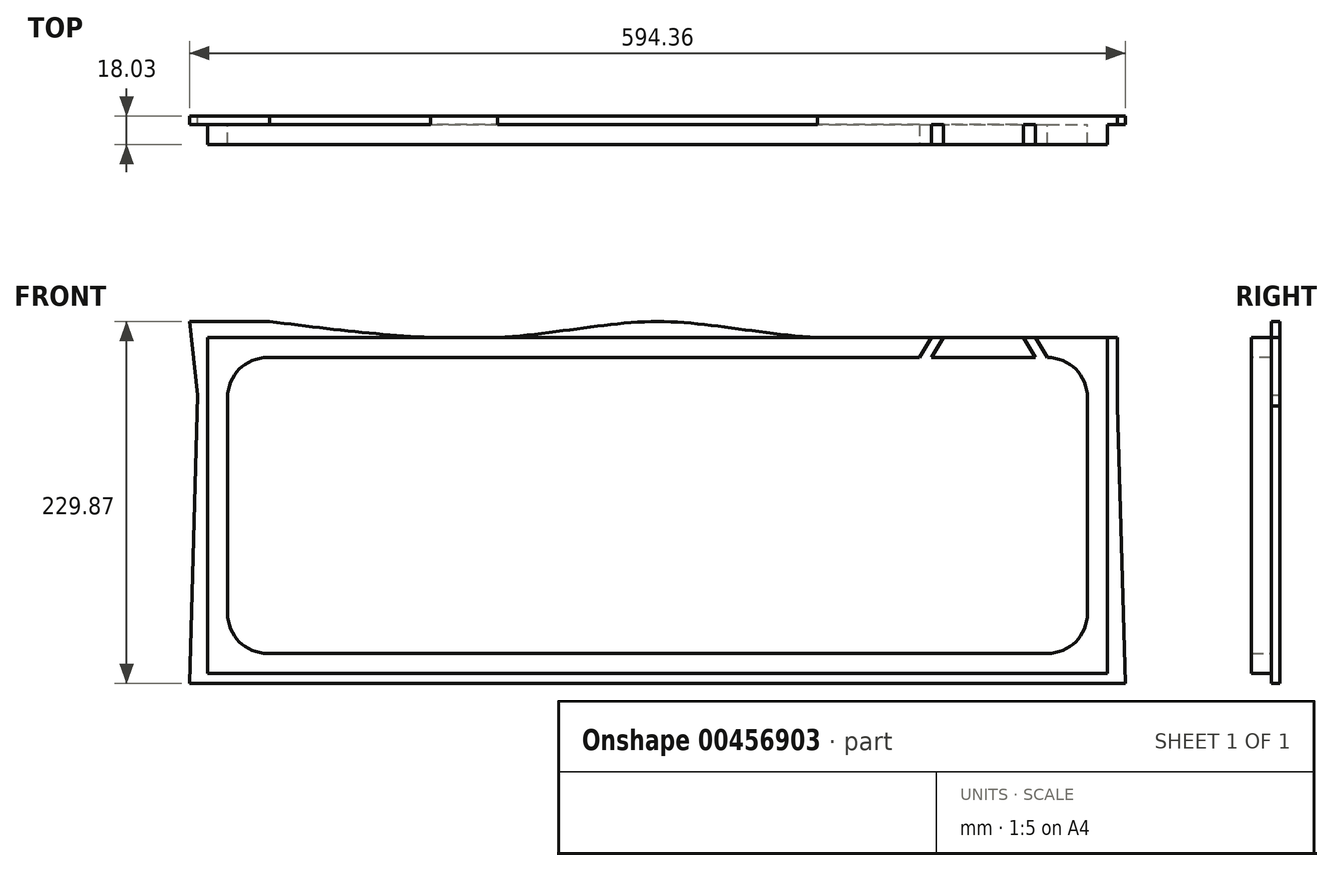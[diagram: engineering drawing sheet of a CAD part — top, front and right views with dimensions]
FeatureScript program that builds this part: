
annotation { "Feature Type Name" : "Feature", "Feature Type Description" : "" }
export const myFeature = defineFeature(function(context is Context, id is Id, definition is map)
    precondition{}
    {
        {
            var Q0;
            Q0=qCreatedBy(makeId("Front.planeOp"),FACE);
            var sketch = newSketch(context, id + "F0", { "sketchPlane" : qUnion([Q0])});
            skLineSegment(sketch, "E0.bottom", {"start": v(0, 0) * mm, "end": v(-584.2, 0) * mm});
            skLineSegment(sketch, "E0.top", {"start": v(0, 219.7) * mm, "end": v(-584.2, 219.7) * mm});
            skLineSegment(sketch, "E0.left", {"start": v(0, 0) * mm, "end": v(0, 219.7) * mm});
            skLineSegment(sketch, "E0.right", {"start": v(-584.2, 0) * mm, "end": v(-584.2, 219.7) * mm});
            skPoint(sketch, "E1", {"position": v(-292.1, 219.7) * mm});
            skSolve(sketch);
        }
        {
            var Q0;
            Q0=makeQuery(id+"F0.imprint","IMPRINT",FACE,{"disambiguationData":[TD([[makeQuery(id+"F0.imprint","IMPRINT",EDGE,{"derivedFrom":sQuery(id+"F0.wireOp",EDGE,"E0.bottom")}),-1.0]])]});
            extrude(context, id + "F1", {"entities" : qUnion([Q0]), "depth" : 5.33 * mm});
        }
        {
            var Q0;
            Q0=makeQuery(id+"F1.opExtrude","CAP_FACE",FACE,{"disambiguationData":[OSD([sQuery(id+"F0.wireOp",EDGE,"E0.bottom"),sQuery(id+"F0.wireOp",EDGE,"E0.top"),sQuery(id+"F0.wireOp",EDGE,"E0.left"),sQuery(id+"F0.wireOp",EDGE,"E0.right")])],"isStart":false});
            var sketch = newSketch(context, id + "F2", { "sketchPlane" : qUnion([Q0])});
            skLineSegment(sketch, "E2", {"start": v(-577.85, 219.7) * mm, "end": v(-577.85, 6.35) * mm});
            skLineSegment(sketch, "E3", {"start": v(-577.85, 6.35) * mm, "end": v(-6.35, 6.35) * mm});
            skLineSegment(sketch, "E4", {"start": v(-6.35, 6.35) * mm, "end": v(-6.35, 219.71) * mm});
            skLineSegment(sketch, "E5", {"start": v(-6.35, 219.71) * mm, "end": v(-577.85, 219.7) * mm});
            skLineSegment(sketch, "E6", {"start": v(-565.15, 207) * mm, "end": v(-565.15, 19.05) * mm});
            skLineSegment(sketch, "E7", {"start": v(-565.15, 19.05) * mm, "end": v(-19.05, 19.05) * mm});
            skLineSegment(sketch, "E8", {"start": v(-19.05, 19.05) * mm, "end": v(-19.05, 207.01) * mm});
            skLineSegment(sketch, "E9", {"start": v(-19.05, 207.01) * mm, "end": v(-565.15, 207) * mm});
            skSolve(sketch);
        }
        {
            var Q0;
            Q0=makeQuery(id+"F2.imprint","IMPRINT",FACE,{"disambiguationData":[TD([[makeQuery(id+"F2.imprint","IMPRINT",EDGE,{"derivedFrom":sQuery(id+"F2.wireOp",EDGE,"E2")}),1.0]])]});
            extrude(context, id + "F3", {"entities" : qUnion([Q0]), "operationType" : NewBodyOperationType.ADD, "depth" : 12.7 * mm});
        }
        {
            var Q0;
            Q0=makeQuery(id+"F3.opExtrude","SWEPT_EDGE",EDGE,{"disambiguationData":[OSD([sQuery(id+"F2.wireOp",EDGE,"E6"),sQuery(id+"F2.wireOp",EDGE,"E9")])]});
            var Q1;
            Q1=makeQuery(id+"F3.opExtrude","SWEPT_EDGE",EDGE,{"disambiguationData":[OSD([sQuery(id+"F2.wireOp",EDGE,"E8"),sQuery(id+"F2.wireOp",EDGE,"E9")])]});
            var Q2;
            Q2=makeQuery(id+"F3.opExtrude","SWEPT_EDGE",EDGE,{"disambiguationData":[OSD([sQuery(id+"F2.wireOp",EDGE,"E7"),sQuery(id+"F2.wireOp",EDGE,"E8")])]});
            var Q3;
            Q3=makeQuery(id+"F3.opExtrude","SWEPT_EDGE",EDGE,{"disambiguationData":[OSD([sQuery(id+"F2.wireOp",EDGE,"E6"),sQuery(id+"F2.wireOp",EDGE,"E7")])]});
            fillet(context, id + "F4", {"entities" : qUnion([Q0, Q1, Q2, Q3]), "radius" : 25.4 * mm, "tangentPropagation" : true, "allowEdgeOverflow" : false});
        }
        {
            var Q0;
            Q0=makeQuery(id+"F3.opExtrude","CAP_FACE",FACE,{"disambiguationData":[OSD([sQuery(id+"F2.wireOp",EDGE,"E2"),sQuery(id+"F2.wireOp",EDGE,"E3"),sQuery(id+"F2.wireOp",EDGE,"E4"),sQuery(id+"F2.wireOp",EDGE,"E5"),sQuery(id+"F2.wireOp",EDGE,"E6"),sQuery(id+"F2.wireOp",EDGE,"E7"),sQuery(id+"F2.wireOp",EDGE,"E8"),sQuery(id+"F2.wireOp",EDGE,"E9")])],"isStart":false});
            var sketch = newSketch(context, id + "F5", { "sketchPlane" : qUnion([Q0])});
            skPoint(sketch, "E10", {"position": v(-118.11, 219.7) * mm});
            skPoint(sketch, "E11", {"position": v(-110.5, 219.7) * mm});
            skPoint(sketch, "E12", {"position": v(-59.69, 219.7) * mm});
            skPoint(sketch, "E13", {"position": v(-52.07, 219.7) * mm});
            skPoint(sketch, "E14", {"position": v(-376.28, 272.75) * mm});
            skPoint(sketch, "E15", {"position": v(-12.7, 0) * mm});
            skPoint(sketch, "E16", {"position": v(-20.32, 0) * mm});
            skLineSegment(sketch, "E17", {"start": v(-20.32, 0) * mm, "end": v(-12.7, 0) * mm});
            skPoint(sketch, "E18", {"position": v(-118.11, 207.01) * mm});
            skPoint(sketch, "E19", {"position": v(-125.73, 207.01) * mm});
            skLineSegment(sketch, "E20", {"start": v(-125.73, 207.01) * mm, "end": v(-118.11, 219.7) * mm});
            skLineSegment(sketch, "E21", {"start": v(-125.73, 207.01) * mm, "end": v(-118.11, 207.01) * mm});
            skLineSegment(sketch, "E22", {"start": v(-118.11, 207.01) * mm, "end": v(-110.5, 219.7) * mm});
            skLineSegment(sketch, "E23", {"start": v(-118.11, 219.7) * mm, "end": v(-110.5, 219.7) * mm});
            skLineSegment(sketch, "E24", {"start": v(-59.69, 219.7) * mm, "end": v(-52.07, 219.7) * mm});
            skLineSegment(sketch, "E25", {"start": v(-110.5, 219.7) * mm, "end": v(-59.69, 219.7) * mm});
            skLineSegment(sketch, "E26", {"start": v(-59.69, 219.7) * mm, "end": v(-110.5, 219.7) * mm});
            skLineSegment(sketch, "E27", {"start": v(-110.5, 219.7) * mm, "end": v(-113.58, 214.56) * mm});
            skPoint(sketch, "E28", {"position": v(-44.45, 207.01) * mm});
            skPoint(sketch, "E29", {"position": v(-52.07, 207.01) * mm});
            skLineSegment(sketch, "E30", {"start": v(-59.69, 219.7) * mm, "end": v(-52.07, 207.01) * mm});
            skLineSegment(sketch, "E31", {"start": v(-52.07, 219.7) * mm, "end": v(-44.45, 207.01) * mm});
            skLineSegment(sketch, "E32", {"start": v(-52.07, 207.01) * mm, "end": v(-44.45, 207.01) * mm});
            skLineSegment(sketch, "E33", {"start": v(-52.07, 219.7) * mm, "end": v(-59.69, 219.7) * mm});
            skPoint(sketch, "E34", {"position": v(-56.6, 214.56) * mm});
            skLineSegment(sketch, "E35", {"start": v(-113.58, 214.56) * mm, "end": v(-56.6, 214.56) * mm});
            skSolve(sketch);
        }
        {
            var Q0;
            Q0=makeQuery(id+"F5.imprint","IMPRINT",FACE,{"disambiguationData":[TD([[makeQuery(id+"F5.imprint","IMPRINT",EDGE,{"derivedFrom":sQuery(id+"F5.wireOp",EDGE,"E20")}),-1.0]])]});
            var Q1;
            {var subQ8=sQuery(id+"F5.wireOp",EDGE,"RZINdJYM-ykuw-GilU-JIjt-DnibDYUsXZuo");Q1=makeQuery(id+"F5.imprint","IMPRINT",FACE,{"disambiguationData":[TD([[makeQuery(id+"F5.imprint","IMPRINT",EDGE,{"derivedFrom":subQ8}),1.0]])]});}
            var Q2;
            Q2=makeQuery(id+"F5.imprint","IMPRINT",FACE,{"disambiguationData":[TD([[makeQuery(id+"F5.imprint","IMPRINT",EDGE,{"derivedFrom":sQuery(id+"F5.wireOp",EDGE,"RZINdJYM-ykuw-GilU-JIjt-DnibDYUsXZuo")}),-1.0]])]});
            var Q3;
            Q3=makeQuery(id+"F5.imprint","IMPRINT",FACE,{"disambiguationData":[TD([[makeQuery(id+"F5.imprint","IMPRINT",EDGE,{"derivedFrom":sQuery(id+"F5.wireOp",EDGE,"NQJIxGkc-Vixr-o2zM-VUe3-bVQ5EoZFKsab")}),1.0]])]});
            var Q4;
            Q4=makeQuery(id+"F5.imprint","IMPRINT",FACE,{"disambiguationData":[TD([[makeQuery(id+"F5.imprint","IMPRINT",EDGE,{"derivedFrom":sQuery(id+"F5.wireOp",EDGE,"E30")}),1.0]])]});
            var Q5;
            {var subQ0=sQuery(id+"F5.wireOp",EDGE,"E26");Q5=makeQuery(id+"F5.imprint","IMPRINT",FACE,{"disambiguationData":[TD([[makeQuery(id+"F5.imprint","IMPRINT",EDGE,{"derivedFrom":subQ0}),1.0]])]});}
            extrude(context, id + "F6", {"entities" : qUnion([Q0, Q1, Q2, Q3, Q4, Q5]), "operationType" : NewBodyOperationType.REMOVE, "oppositeDirection" : true, "depth" : 12.7 * mm});
        }
        {
            var Q0;
            Q0=makeQuery(id+"F1.opExtrude","CAP_FACE",FACE,{"disambiguationData":[OSD([sQuery(id+"F0.wireOp",EDGE,"E0.bottom"),sQuery(id+"F0.wireOp",EDGE,"E0.top"),sQuery(id+"F0.wireOp",EDGE,"E0.left"),sQuery(id+"F0.wireOp",EDGE,"E0.right")])],"isStart":true});
            var sketch = newSketch(context, id + "F7", { "sketchPlane" : qUnion([Q0])});
            skLineSegment(sketch, "E36", {"start": v(0, 0) * mm, "end": v(-5.08, 0) * mm});
            skLineSegment(sketch, "E37", {"start": v(-5.08, 0) * mm, "end": v(-5.08, 229.87) * mm});
            skLineSegment(sketch, "E38", {"start": v(-5.08, 229.87) * mm, "end": v(589.28, 229.87) * mm});
            skLineSegment(sketch, "E39", {"start": v(589.28, 229.87) * mm, "end": v(589.28, 0) * mm});
            skLineSegment(sketch, "E40", {"start": v(589.28, 0) * mm, "end": v(584.2, 0) * mm});
            skPoint(sketch, "E41", {"position": v(589.28, 114.93) * mm});
            skPoint(sketch, "E42", {"position": v(584.2, 109.85) * mm});
            skPoint(sketch, "E43", {"position": v(292.1, 229.87) * mm});
            skPoint(sketch, "E44", {"position": v(292.1, 219.7) * mm});
            skPoint(sketch, "E45", {"position": v(-5.08, 114.93) * mm});
            skPoint(sketch, "E46", {"position": v(0, 109.85) * mm});
            skPoint(sketch, "E47", {"position": v(538.48, 229.87) * mm});
            skPoint(sketch, "E48", {"position": v(45.72, 229.87) * mm});
            skPoint(sketch, "E49", {"position": v(-5.08, 191.77) * mm});
            skPoint(sketch, "E50", {"position": v(589.28, 191.77) * mm});
            skPoint(sketch, "E51", {"position": v(584.2, 183.25) * mm});
            skPoint(sketch, "E52", {"position": v(0, 176.13) * mm});
            skPoint(sketch, "E53", {"position": v(589.28, 63.5) * mm});
            skPoint(sketch, "E54", {"position": v(-5.08, 63.5) * mm});
            skPoint(sketch, "E55", {"position": v(0, 219.7) * mm});
            skPoint(sketch, "E56", {"position": v(584.2, 219.7) * mm});
            skPoint(sketch, "E57", {"position": v(393.7, 219.7) * mm});
            skPoint(sketch, "E58", {"position": v(190.5, 219.7) * mm});
            skFitSpline(sketch, "E59", {"points": [v(538.48, 229.87) * mm, v(393.7, 219.7) * mm, v(292.1, 229.87) * mm, v(190.5, 219.7) * mm, v(45.72, 229.87) * mm], "startDerivative": vector(-556.08, -69.34) * mm, "endDerivative": vector(-556.08, 69.34) * mm});
            skLineSegment(sketch, "E60", {"start": v(-5.08, 229.87) * mm, "end": v(0, 176.13) * mm});
            skLineSegment(sketch, "E61", {"start": v(584.2, 183.25) * mm, "end": v(589.28, 229.87) * mm});
            skLineSegment(sketch, "E62", {"start": v(-5.08, 0) * mm, "end": v(0, 176.13) * mm});
            skLineSegment(sketch, "E63", {"start": v(584.2, 183.25) * mm, "end": v(589.28, 0) * mm});
            skSolve(sketch);
        }
        {
            var Q0;
            {var subQ3=sQuery(id+"F7.wireOp",EDGE,"1cZOkDzA-QB0z-r1xi-g2sP-Uw8mw8TRGHdY");Q0=makeQuery(id+"F7.imprint","IMPRINT",FACE,{"disambiguationData":[TD([[makeQuery(id+"F7.imprint","IMPRINT",EDGE,{"derivedFrom":subQ3}),-1.0]])]});}
            var Q1;
            {var subQ0=sQuery(id+"F7.wireOp",EDGE,"E59");var subQ1=makeQuery(id+"F7.imprint","INTERSECT",VERTEX,{"disambiguationData":[OD(2.0)],"derivedFrom":[sQuery(id+"F7.wireOp",EDGE,"E38"),subQ0]});Q1=makeQuery(id+"F7.imprint","IMPRINT",FACE,{"disambiguationData":[TD([[makeQuery(id+"F7.imprint","IMPRINT",EDGE,{"disambiguationData":[TD([[subQ1,1.0]])],"derivedFrom":subQ0}),1.0]])]});}
            var Q2;
            {var subQ1=sQuery(id+"F7.wireOp",EDGE,"E38");var subQ7=sQuery(id+"F7.wireOp",EDGE,"E59");var subQ8=makeQuery(id+"F7.imprint","INTERSECT",VERTEX,{"disambiguationData":[OD(1.0)],"derivedFrom":[subQ1,subQ7]});Q2=makeQuery(id+"F7.imprint","IMPRINT",FACE,{"disambiguationData":[TD([[makeQuery(id+"F7.imprint","IMPRINT",EDGE,{"disambiguationData":[TD([[subQ8,1.0]])],"derivedFrom":subQ7}),1.0]])]});}
            var Q3;
            {var subQ0=sQuery(id+"F7.wireOp",EDGE,"E40");Q3=makeQuery(id+"F7.imprint","IMPRINT",FACE,{"disambiguationData":[TD([[makeQuery(id+"F7.imprint","IMPRINT",EDGE,{"derivedFrom":subQ0}),-1.0]])]});}
            var Q4;
            {var subQ7=sQuery(id+"F7.wireOp",EDGE,"E61");Q4=makeQuery(id+"F7.imprint","IMPRINT",FACE,{"disambiguationData":[TD([[makeQuery(id+"F7.imprint","IMPRINT",EDGE,{"derivedFrom":subQ7}),1.0]])]});}
            var Q5;
            {var subQ0=sQuery(id+"F7.wireOp",EDGE,"E36");Q5=makeQuery(id+"F7.imprint","IMPRINT",FACE,{"disambiguationData":[TD([[makeQuery(id+"F7.imprint","IMPRINT",EDGE,{"derivedFrom":subQ0}),-1.0]])]});}
            extrude(context, id + "F8", {"entities" : qUnion([Q0, Q1, Q2, Q3, Q4, Q5]), "operationType" : NewBodyOperationType.ADD, "depth" : -5.33 * mm});
        }
    });
